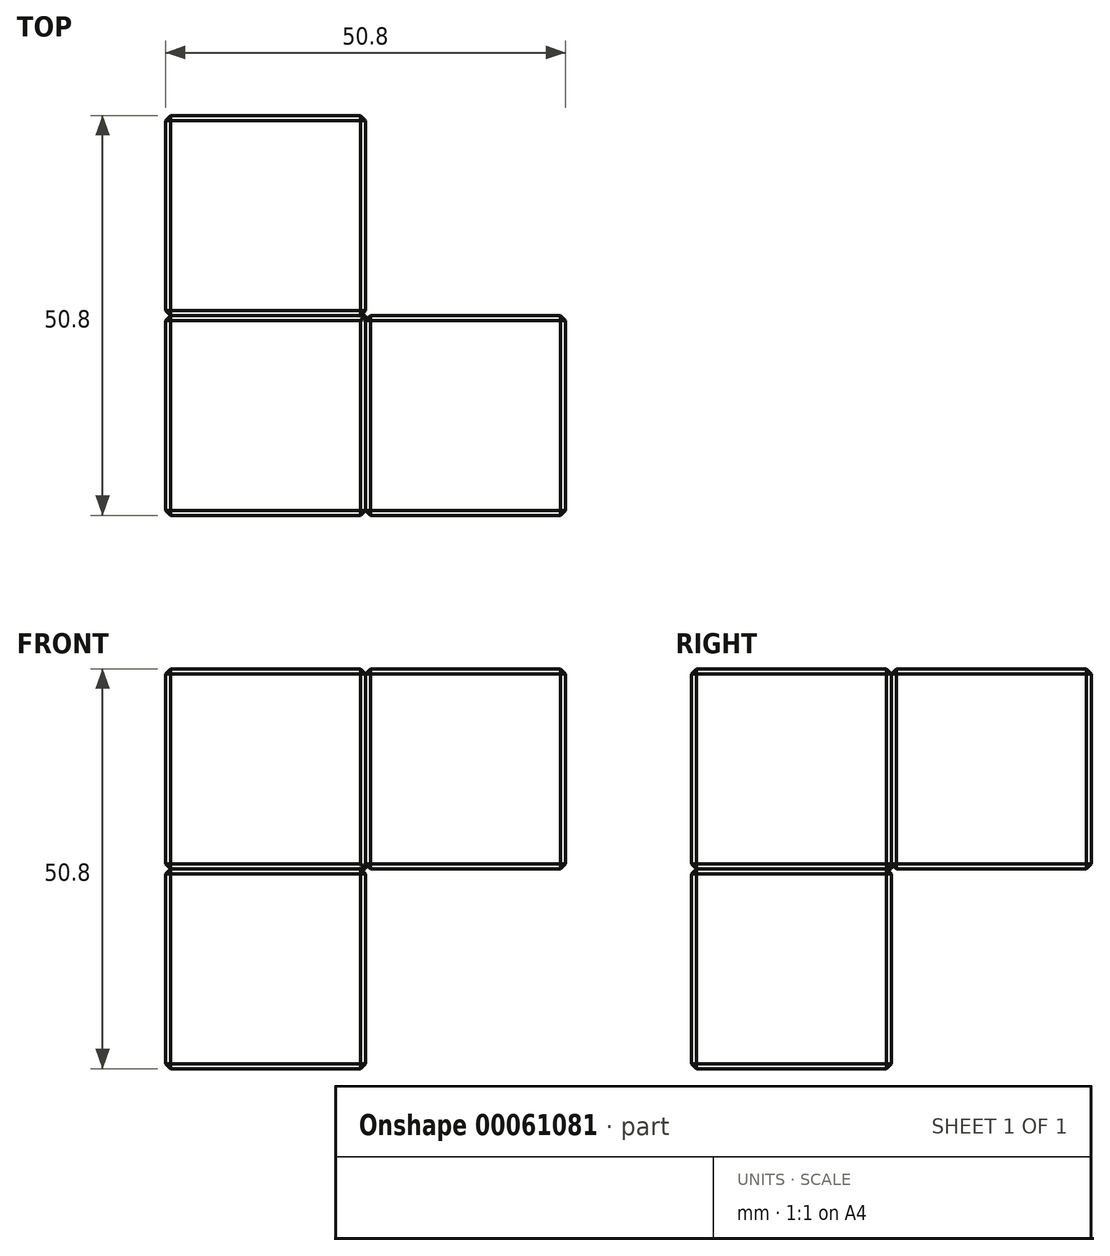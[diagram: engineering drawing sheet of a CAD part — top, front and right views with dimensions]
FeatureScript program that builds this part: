
annotation { "Feature Type Name" : "Feature", "Feature Type Description" : "" }
export const myFeature = defineFeature(function(context is Context, id is Id, definition is map)
    precondition{}
    {
        {
            var Q0;
            Q0=qCreatedBy(makeId("Top.planeOp"),FACE);
            var sketch = newSketch(context, id + "F0", { "sketchPlane" : qUnion([Q0])});
            skLineSegment(sketch, "E0.rect.bottom", {"start": v(-12.7, 12.7) * mm, "end": v(12.7, 12.7) * mm});
            skLineSegment(sketch, "E0.rect.top", {"start": v(-12.7, -12.7) * mm, "end": v(12.7, -12.7) * mm});
            skLineSegment(sketch, "E0.rect.left", {"start": v(-12.7, 12.7) * mm, "end": v(-12.7, -12.7) * mm});
            skLineSegment(sketch, "E0.rect.right", {"start": v(12.7, 12.7) * mm, "end": v(12.7, -12.7) * mm});
            skPoint(sketch, "E0.rect.middle", {"position": v(0, 0) * mm});
            skLineSegment(sketch, "E1.top", {"start": v(-12.7, 38.1) * mm, "end": v(12.7, 38.1) * mm});
            skLineSegment(sketch, "E1.left", {"start": v(-12.7, 12.7) * mm, "end": v(-12.7, 38.1) * mm});
            skLineSegment(sketch, "E1.right", {"start": v(12.7, 12.7) * mm, "end": v(12.7, 38.1) * mm});
            skLineSegment(sketch, "E2.bottom", {"start": v(12.7, 12.7) * mm, "end": v(38.1, 12.7) * mm});
            skLineSegment(sketch, "E2.top", {"start": v(12.7, -12.7) * mm, "end": v(38.1, -12.7) * mm});
            skLineSegment(sketch, "E2.right", {"start": v(38.1, 12.7) * mm, "end": v(38.1, -12.7) * mm});
            skSolve(sketch);
        }
        {
            var Q0;
            Q0=makeQuery(id+"F0.imprint","IMPRINT",FACE,{"disambiguationData":[TD([[makeQuery(id+"F0.imprint","IMPRINT",EDGE,{"derivedFrom":sQuery(id+"F0.wireOp",EDGE,"E2.bottom")}),-1.0]])]});
            extrude(context, id + "F1", {"entities" : qUnion([Q0]), "depth" : 25.4 * mm});
        }
        {
            var Q0;
            Q0=makeQuery(id+"F0.imprint","IMPRINT",FACE,{"disambiguationData":[TD([[makeQuery(id+"F0.imprint","IMPRINT",EDGE,{"derivedFrom":sQuery(id+"F0.wireOp",EDGE,"E0.rect.top")}),1.0]])]});
            extrude(context, id + "F2", {"entities" : qUnion([Q0]), "depth" : 25.4 * mm});
        }
        {
            var Q0;
            Q0=makeQuery(id+"F0.imprint","IMPRINT",FACE,{"disambiguationData":[TD([[makeQuery(id+"F0.imprint","IMPRINT",EDGE,{"derivedFrom":sQuery(id+"F0.wireOp",EDGE,"E0.rect.bottom")}),1.0]])]});
            extrude(context, id + "F3", {"entities" : qUnion([Q0]), "depth" : 25.4 * mm});
        }
        {
            var Q0;
            Q0=makeQuery(id+"F0.imprint","IMPRINT",FACE,{"disambiguationData":[TD([[makeQuery(id+"F0.imprint","IMPRINT",EDGE,{"derivedFrom":sQuery(id+"F0.wireOp",EDGE,"E0.rect.top")}),1.0]])]});
            extrude(context, id + "F4", {"entities" : qUnion([Q0]), "oppositeDirection" : true, "depth" : 25.4 * mm});
        }
        {
            var Q0;
            Q0=makeQuery(id+"F1.opExtrude","CAP_FACE",FACE,{"disambiguationData":[OSD([sQuery(id+"F0.wireOp",EDGE,"E2.bottom"),sQuery(id+"F0.wireOp",EDGE,"E2.top"),sQuery(id+"F0.wireOp",EDGE,"E0.rect.right"),sQuery(id+"F0.wireOp",EDGE,"E2.right")])],"isStart":true});
            var Q1;
            Q1=makeQuery(id+"F1.opExtrude","SWEPT_FACE",FACE,{"disambiguationData":[OSD([sQuery(id+"F0.wireOp",EDGE,"E2.top")])]});
            var Q2;
            Q2=makeQuery(id+"F2.opExtrude","SWEPT_FACE",FACE,{"disambiguationData":[OSD([sQuery(id+"F0.wireOp",EDGE,"E0.rect.top")])]});
            var Q3;
            Q3=makeQuery(id+"F4.opExtrude","SWEPT_FACE",FACE,{"disambiguationData":[OSD([sQuery(id+"F0.wireOp",EDGE,"E0.rect.top")])]});
            var Q4;
            Q4=makeQuery(id+"F4.opExtrude","SWEPT_FACE",FACE,{"disambiguationData":[OSD([sQuery(id+"F0.wireOp",EDGE,"E0.rect.right")])]});
            var Q5;
            Q5=makeQuery(id+"F1.opExtrude","CAP_FACE",FACE,{"disambiguationData":[OSD([sQuery(id+"F0.wireOp",EDGE,"E2.bottom"),sQuery(id+"F0.wireOp",EDGE,"E2.top"),sQuery(id+"F0.wireOp",EDGE,"E0.rect.right"),sQuery(id+"F0.wireOp",EDGE,"E2.right")])],"isStart":false});
            var Q6;
            Q6=makeQuery(id+"F2.opExtrude","CAP_FACE",FACE,{"disambiguationData":[OSD([sQuery(id+"F0.wireOp",EDGE,"E0.rect.top"),sQuery(id+"F0.wireOp",EDGE,"E0.rect.left"),sQuery(id+"F0.wireOp",EDGE,"E0.rect.bottom"),sQuery(id+"F0.wireOp",EDGE,"E0.rect.right")])],"isStart":false});
            var Q7;
            Q7=makeQuery(id+"F3.opExtrude","CAP_FACE",FACE,{"disambiguationData":[OSD([sQuery(id+"F0.wireOp",EDGE,"E0.rect.bottom"),sQuery(id+"F0.wireOp",EDGE,"E1.top"),sQuery(id+"F0.wireOp",EDGE,"E1.left"),sQuery(id+"F0.wireOp",EDGE,"E1.right")])],"isStart":false});
            var Q8;
            Q8=makeQuery(id+"F3.opExtrude","SWEPT_FACE",FACE,{"disambiguationData":[OSD([sQuery(id+"F0.wireOp",EDGE,"E1.right")])]});
            var Q9;
            Q9=makeQuery(id+"F1.opExtrude","SWEPT_FACE",FACE,{"disambiguationData":[OSD([sQuery(id+"F0.wireOp",EDGE,"E2.bottom")])]});
            var Q10;
            Q10=makeQuery(id+"F4.opExtrude","SWEPT_FACE",FACE,{"disambiguationData":[OSD([sQuery(id+"F0.wireOp",EDGE,"E0.rect.bottom")])]});
            var Q11;
            Q11=makeQuery(id+"F3.opExtrude","CAP_FACE",FACE,{"disambiguationData":[OSD([sQuery(id+"F0.wireOp",EDGE,"E0.rect.bottom"),sQuery(id+"F0.wireOp",EDGE,"E1.top"),sQuery(id+"F0.wireOp",EDGE,"E1.left"),sQuery(id+"F0.wireOp",EDGE,"E1.right")])],"isStart":true});
            var Q12;
            Q12=makeQuery(id+"F3.opExtrude","SWEPT_FACE",FACE,{"disambiguationData":[OSD([sQuery(id+"F0.wireOp",EDGE,"E1.top")])]});
            var Q13;
            Q13=makeQuery(id+"F3.opExtrude","SWEPT_FACE",FACE,{"disambiguationData":[OSD([sQuery(id+"F0.wireOp",EDGE,"E1.left")])]});
            var Q14;
            Q14=makeQuery(id+"F4.opExtrude","SWEPT_FACE",FACE,{"disambiguationData":[OSD([sQuery(id+"F0.wireOp",EDGE,"E0.rect.left")])]});
            var Q15;
            Q15=makeQuery(id+"F2.opExtrude","SWEPT_FACE",FACE,{"disambiguationData":[OSD([sQuery(id+"F0.wireOp",EDGE,"E0.rect.left")])]});
            chamfer(context, id + "F5", {"entities" : qUnion([Q0, Q1, Q2, Q3, Q4, Q5, Q6, Q7, Q8, Q9, Q10, Q11, Q12, Q13, Q14, Q15]), "width" : 0.64 * mm, "tangentPropagation" : true});
        }
    });
